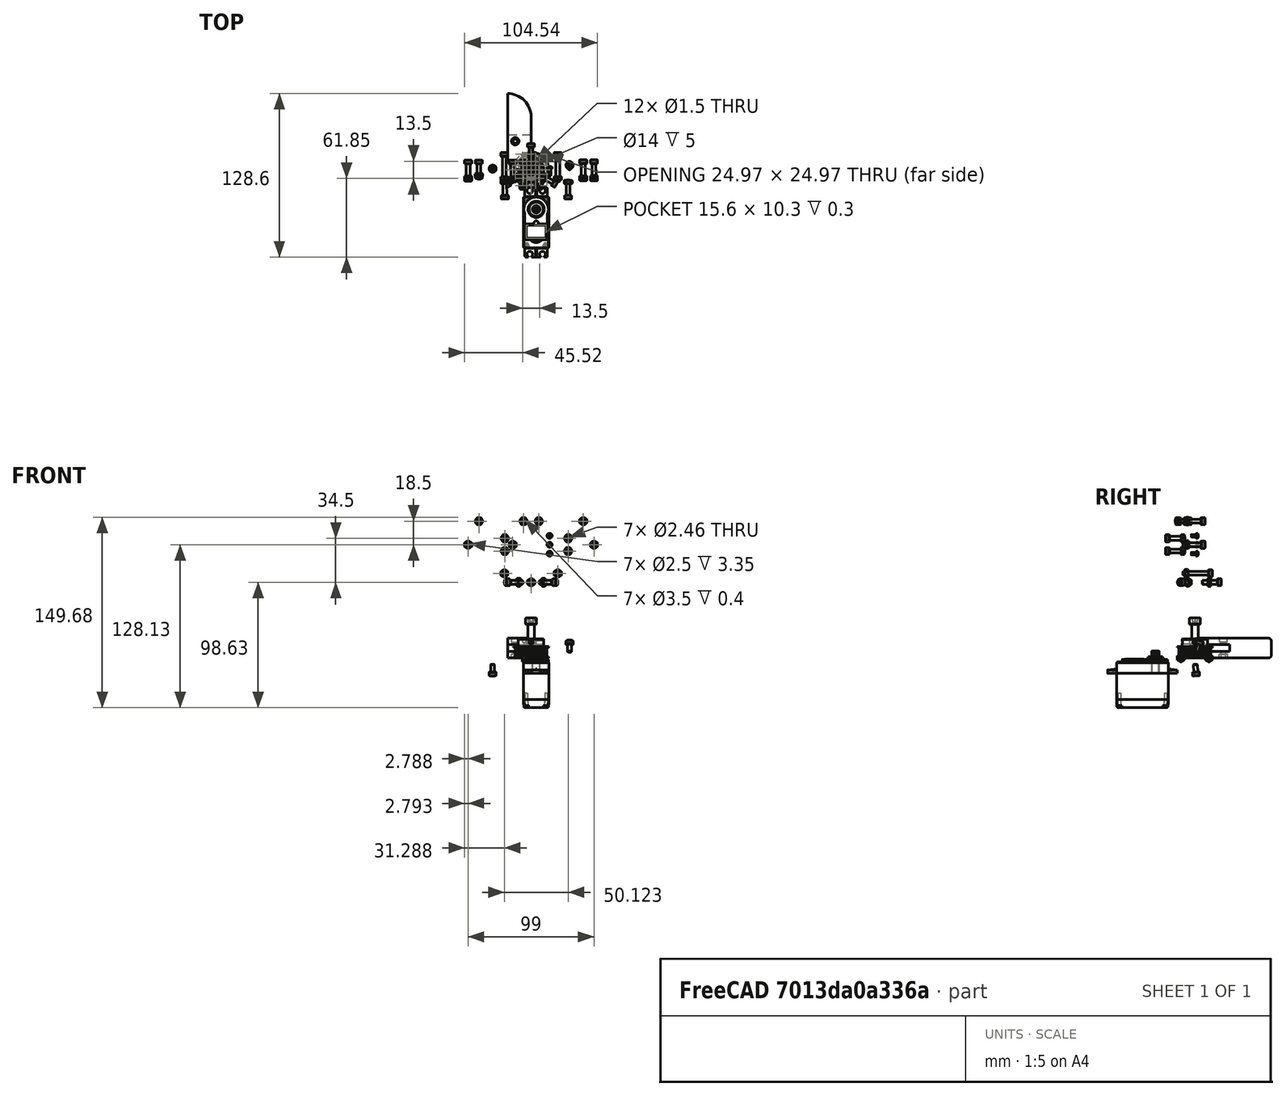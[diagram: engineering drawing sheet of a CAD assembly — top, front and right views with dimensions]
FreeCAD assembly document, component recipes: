
FREECAD ASSEMBLY — COMPONENT RECIPES ("AssemblyArt56")

This assembly document has 5 components, labeled P0..P4 below (a component is one placed body or linked part). 0 of them carry a construction recipe — the FreeCAD feature program that regenerates the part from scratch, quoted from this document or its linked companion documents; the rest are supplied as boundary geometry only. No exploded tour is included for this assembly.
COMPONENT P0 — geometry summary ("Bearing_625ZZ"; no construction recipe available for this part):
  bounding box: 16.0 x 16.0 x 5.0 mm
  tessellated surface: 4,788 triangles
  volume: 876 mm^3 (68% of its bounding box)
  symmetry: 2-fold rotationally symmetric about the x axis; 2-fold rotationally symmetric about the y axis; revolution-symmetric about the z axis through its bounding-box center; mirror-symmetric across its x mid-plane, y mid-plane, z mid-plane
COMPONENT P1 — geometry summary ("GripperFinger_sym"; no construction recipe available for this part):
  bounding box: 60.0 x 18.5 x 15.5 mm
  tessellated surface: 7,758 triangles
  volume: 12593 mm^3 (73% of its bounding box)
  symmetry: mirror-symmetric across its z mid-plane
COMPONENT P2 — geometry summary ("Pulley_GT2x40"; no construction recipe available for this part):
  bounding box: 28.0 x 28.0 x 15.0 mm
  tessellated surface: 7,246 triangles
  volume: 5901 mm^3 (50% of its bounding box)
COMPONENT P3 — geometry summary ("Servomotor"; no construction recipe available for this part):
  bounding box: 54.6 x 44.5 x 19.8 mm
  tessellated surface: 20,732 triangles
  volume: 30648 mm^3 (64% of its bounding box)
  symmetry: mirror-symmetric across its x mid-plane
COMPONENT P4 — geometry summary ("ServomotorWheelHorn"; no construction recipe available for this part):
  bounding box: 21.0 x 21.0 x 5.5 mm
  tessellated surface: 4,500 triangles
  volume: 854 mm^3 (35% of its bounding box)
  symmetry: 4-fold rotationally symmetric about the z axis; mirror-symmetric across its y mid-plane
PROVENANCE & LICENSES
A FreeCAD (.FCStd) document from a public repository crawl; recipes are the document's own serialized feature recipes (and, for linked parts, companion documents' recipes).
License: as declared in the source repository (recorded in the dataset sidecar).
